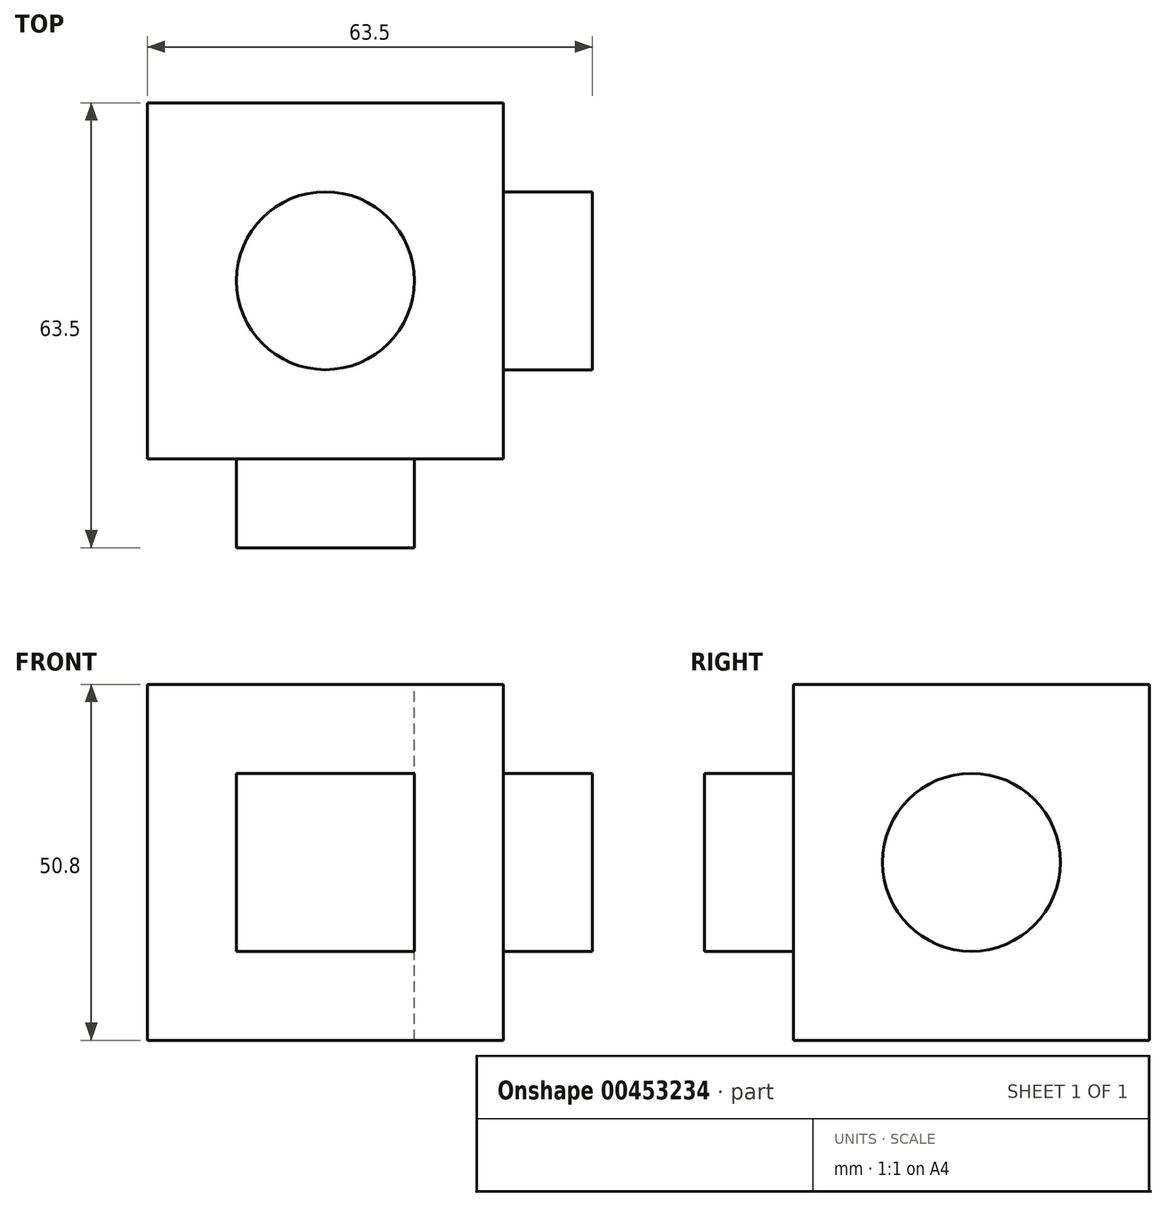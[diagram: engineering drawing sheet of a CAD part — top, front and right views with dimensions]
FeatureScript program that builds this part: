
annotation { "Feature Type Name" : "Feature", "Feature Type Description" : "" }
export const myFeature = defineFeature(function(context is Context, id is Id, definition is map)
    precondition{}
    {
        {
            var Q0;
            Q0=qCreatedBy(makeId("Front.planeOp"),FACE);
            var sketch = newSketch(context, id + "F0", { "sketchPlane" : qUnion([Q0])});
            skLineSegment(sketch, "E0.bottom", {"start": v(25.4, -25.4) * mm, "end": v(-25.4, -25.4) * mm});
            skLineSegment(sketch, "E0.top", {"start": v(25.4, 25.4) * mm, "end": v(-25.4, 25.4) * mm});
            skLineSegment(sketch, "E0.left", {"start": v(25.4, -25.4) * mm, "end": v(25.4, 25.4) * mm});
            skLineSegment(sketch, "E0.right", {"start": v(-25.4, -25.4) * mm, "end": v(-25.4, 25.4) * mm});
            skPoint(sketch, "E0.middle", {"position": v(0, 0) * mm});
            skSolve(sketch);
        }
        {
            var Q0;
            Q0 = qSketchRegion(id + "F0", true);
            extrude(context, id + "F1", {"entities" : qUnion([Q0]), "depth" : 50.8 * mm});
        }
        {
            var Q0;
            Q0=makeQuery(id+"F1.opExtrude","CAP_FACE",FACE,{"disambiguationData":[OSD([sQuery(id+"F0.wireOp",EDGE,"E0.bottom"),sQuery(id+"F0.wireOp",EDGE,"E0.top"),sQuery(id+"F0.wireOp",EDGE,"E0.left"),sQuery(id+"F0.wireOp",EDGE,"E0.right")])],"isStart":false});
            var sketch = newSketch(context, id + "F2", { "sketchPlane" : qUnion([Q0])});
            skLineSegment(sketch, "E1.bottom", {"start": v(12.7, -12.7) * mm, "end": v(-12.7, -12.7) * mm});
            skLineSegment(sketch, "E1.top", {"start": v(12.7, 12.7) * mm, "end": v(-12.7, 12.7) * mm});
            skLineSegment(sketch, "E1.left", {"start": v(12.7, -12.7) * mm, "end": v(12.7, 12.7) * mm});
            skLineSegment(sketch, "E1.right", {"start": v(-12.7, -12.7) * mm, "end": v(-12.7, 12.7) * mm});
            skPoint(sketch, "E1.middle", {"position": v(0, 0) * mm});
            skSolve(sketch);
        }
        {
            var Q0;
            Q0=makeQuery(id+"F1.opExtrude","SWEPT_FACE",FACE,{"disambiguationData":[OSD([sQuery(id+"F0.wireOp",EDGE,"E0.left")])]});
            var sketch = newSketch(context, id + "F3", { "sketchPlane" : qUnion([Q0])});
            skCircle(sketch, "E2", {"center": v(-25.4, 0) * mm, "radius": 12.7 * mm});
            skPoint(sketch, "E2.centerSnap0", {"position": v(-25.4, -25.4) * mm});
            skSolve(sketch);
        }
        {
            var Q0;
            Q0 = qSketchRegion(id + "F3", true);
            extrude(context, id + "F4", {"entities" : qUnion([Q0]), "operationType" : NewBodyOperationType.ADD, "depth" : 12.7 * mm});
        }
        {
            var Q0;
            Q0 = qSketchRegion(id + "F2", true);
            extrude(context, id + "F5", {"entities" : qUnion([Q0]), "operationType" : NewBodyOperationType.ADD, "depth" : 12.7 * mm});
        }
        {
            var Q0;
            Q0=makeQuery(id+"F1.opExtrude","SWEPT_FACE",FACE,{"disambiguationData":[OSD([sQuery(id+"F0.wireOp",EDGE,"E0.top")])]});
            var sketch = newSketch(context, id + "F6", { "sketchPlane" : qUnion([Q0])});
            skCircle(sketch, "E3", {"center": v(0, -25.4) * mm, "radius": 12.7 * mm});
            skPoint(sketch, "E3.centerSnap0", {"position": v(-25.4, -25.4) * mm});
            skSolve(sketch);
        }
        {
            var Q0;
            Q0 = qSketchRegion(id + "F6", true);
            extrude(context, id + "F7", {"entities" : qUnion([Q0]), "operationType" : NewBodyOperationType.REMOVE, "oppositeDirection" : true, "depth" : 94.49 * mm});
        }
    });
